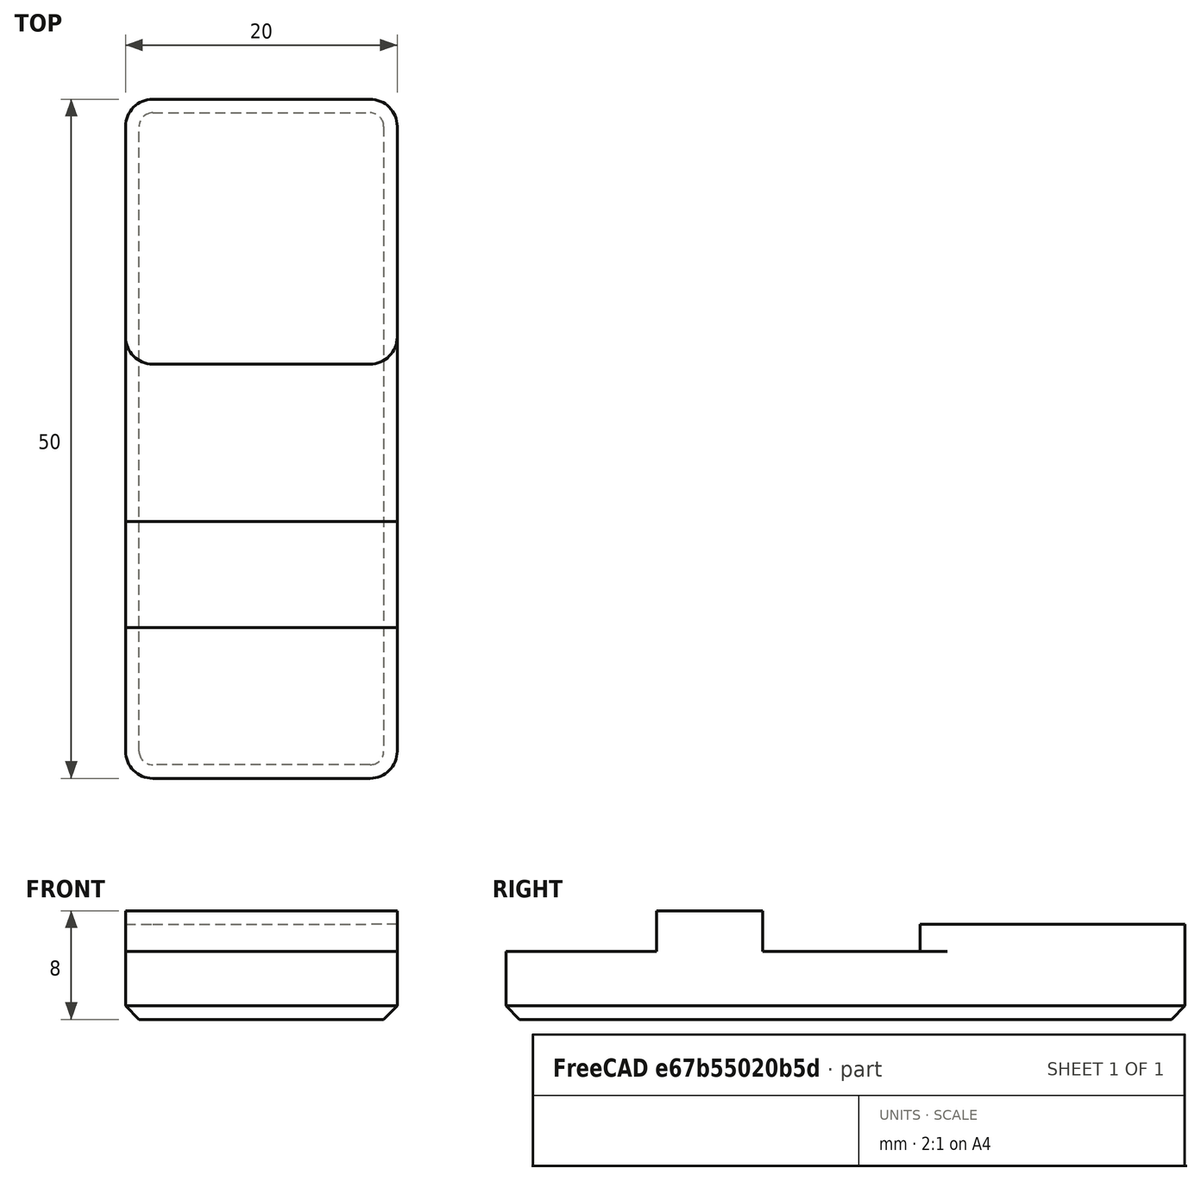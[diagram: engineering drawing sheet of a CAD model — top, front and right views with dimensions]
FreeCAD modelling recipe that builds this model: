
FCSTD DOCUMENT  (FreeCAD 0.19R24291 (Git))
Label: z-motor-plater-aligner
License: Other
LicenseURL: GPL3
objects: Part::Box×3, Part::Fillet×2, Part::Chamfer×1, Part::MultiFuse×1
note: 7 computed .brp shape members not serialized (recipe doc carries the construction recipe); baked Part::Feature solids carry a one-line shape summary decoded from their .brp

FEATURE [Part::Box] Box  label="Cube"
  AttacherType = Attacher::AttachEngine3D
  Height = 5
  Length = 20
  Width = 50
FEATURE [Part::Box] Box001  label="Cube001"
  AttacherType = Attacher::AttachEngine3D
  Height = 3
  Length = 20
  Placement = pos=(0,11.1,5) rot=(0,0,1;0rad)
  Width = 7.8
FEATURE [Part::Box] Box002  label="Cube002"
  AttacherType = Attacher::AttachEngine3D
  Height = 2
  Length = 20
  Placement = pos=(0,30.5,5) rot=(0,0,1;0rad)
  Width = 19.5
FEATURE [Part::Fillet] Fillet
  Base = -> Box
  Edges = 4 edges r=2: [Edge1,Edge3,Edge5,Edge7]
FEATURE [Part::Chamfer] Chamfer
  Base = -> Fillet
  Edges = 8 edges r=1: [Edge3,Edge12,Edge14,Edge16,Edge17,Edge18,Edge19,Edge20]
FEATURE [Part::Fillet] Fillet001
  Base = -> Box002
  Edges = 4 edges r=2: [Edge1,Edge3,Edge5,Edge7]
FEATURE [Part::MultiFuse] Fusion
  Shapes = -> [Fillet001,Chamfer,Box001]
